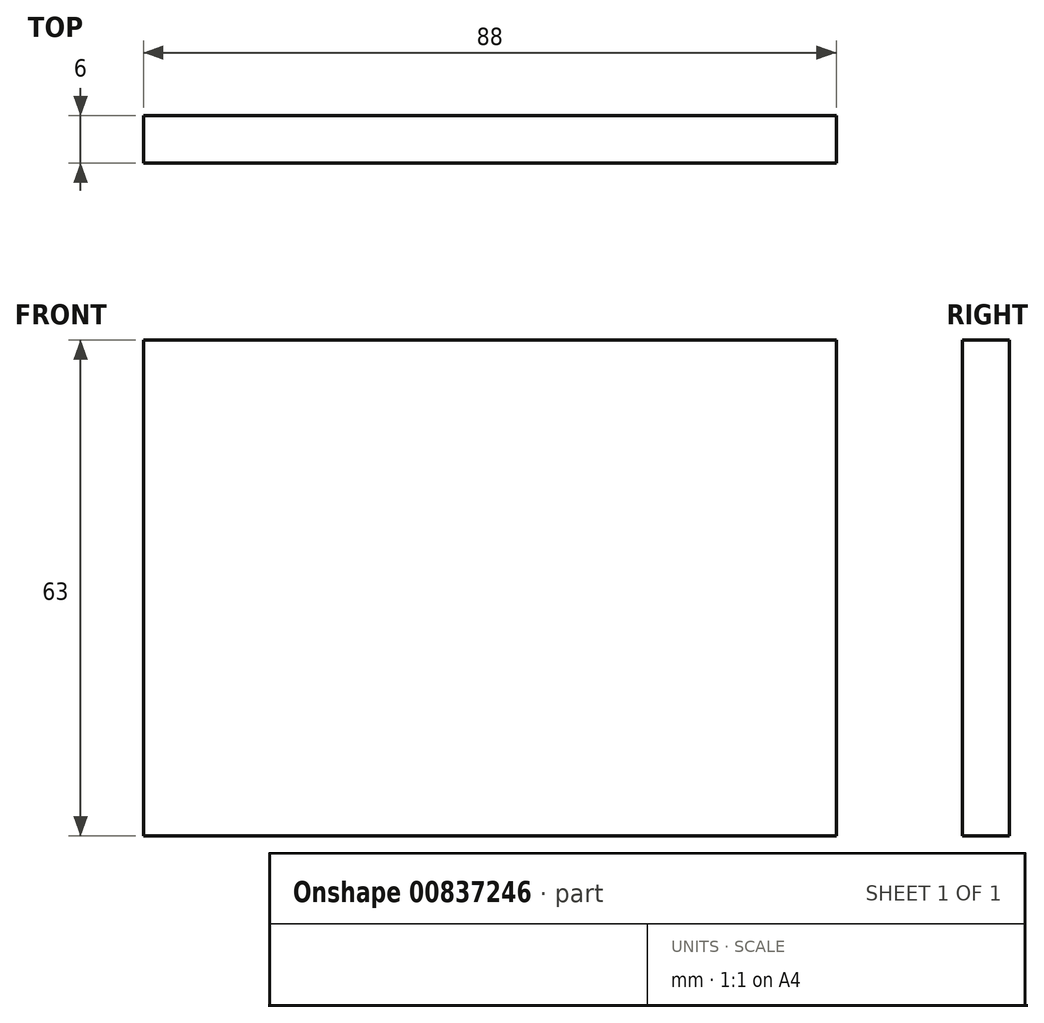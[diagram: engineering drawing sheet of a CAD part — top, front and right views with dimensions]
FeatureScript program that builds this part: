
annotation { "Feature Type Name" : "Feature", "Feature Type Description" : "" }
export const myFeature = defineFeature(function(context is Context, id is Id, definition is map)
    precondition{}
    {
        {
            var Q0;
            Q0=qCreatedBy(makeId("Front.planeOp"),FACE);
            var sketch = newSketch(context, id + "F0", { "sketchPlane" : qUnion([Q0])});
            skLineSegment(sketch, "E0.bottom", {"start": v(44, 31.5) * mm, "end": v(-44, 31.5) * mm});
            skLineSegment(sketch, "E0.top", {"start": v(44, -31.5) * mm, "end": v(-44, -31.5) * mm});
            skLineSegment(sketch, "E0.left", {"start": v(44, 31.5) * mm, "end": v(44, -31.5) * mm});
            skLineSegment(sketch, "E0.right", {"start": v(-44, 31.5) * mm, "end": v(-44, -31.5) * mm});
            skPoint(sketch, "E0.middle", {"position": v(0, 0) * mm});
            skSolve(sketch);
        }
        {
            var Q0;
            Q0 = qSketchRegion(id + "F0", true);
            extrude(context, id + "F1", {"entities" : qUnion([Q0]), "depth" : 6 * mm, "offsetDistance" : 25.4 * mm});
        }
    });
